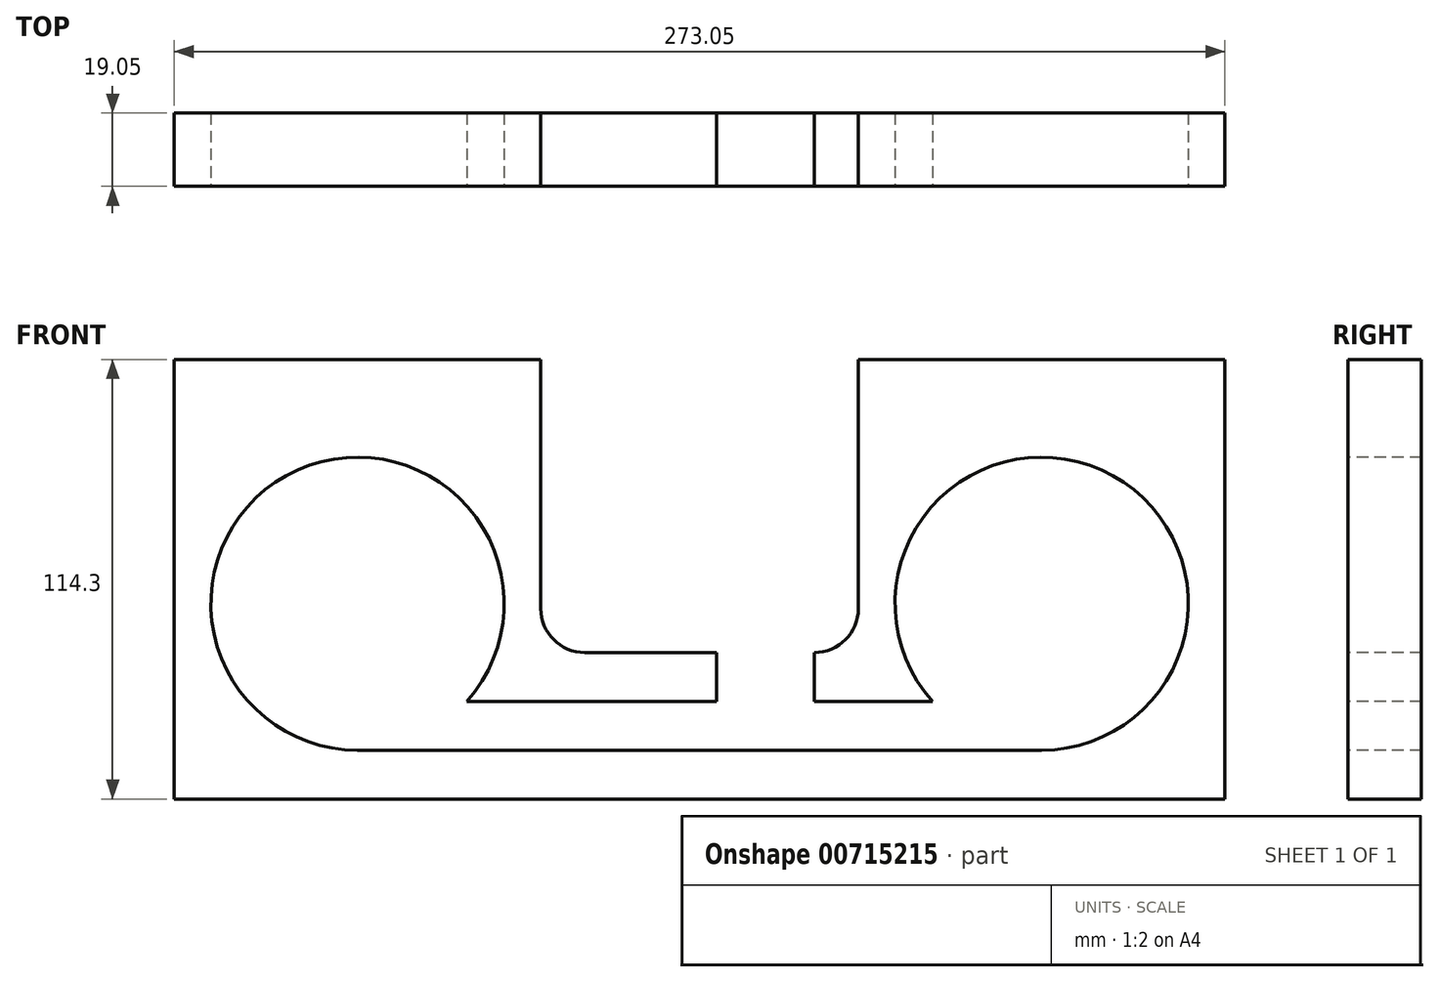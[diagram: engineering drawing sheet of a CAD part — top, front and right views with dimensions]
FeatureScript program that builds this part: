
annotation { "Feature Type Name" : "Feature", "Feature Type Description" : "" }
export const myFeature = defineFeature(function(context is Context, id is Id, definition is map)
    precondition{}
    {
        {
            var Q0;
            Q0=qCreatedBy(makeId("Front.planeOp"),FACE);
            var sketch = newSketch(context, id + "F0", { "sketchPlane" : qUnion([Q0])});
            skLineSegment(sketch, "E0.bottom", {"start": v(0, 0) * mm, "end": v(273.05, 0) * mm});
            skLineSegment(sketch, "E0.top", {"start": v(0, 114.3) * mm, "end": v(273.05, 114.3) * mm});
            skLineSegment(sketch, "E0.left", {"start": v(0, 0) * mm, "end": v(0, 114.3) * mm});
            skLineSegment(sketch, "E0.right", {"start": v(273.05, 0) * mm, "end": v(273.05, 114.3) * mm});
            skSolve(sketch);
        }
        {
            var Q0;
            Q0 = qSketchRegion(id + "F0", true);
            extrude(context, id + "F1", {"entities" : qUnion([Q0]), "depth" : 19.05 * mm, "offsetDistance" : 25.4 * mm});
        }
        {
            var Q0;
            Q0=makeQuery(id+"F1.opExtrude","CAP_FACE",FACE,{"disambiguationData":[OSD([sQuery(id+"F0.wireOp",EDGE,"E0.bottom"),sQuery(id+"F0.wireOp",EDGE,"E0.top"),sQuery(id+"F0.wireOp",EDGE,"E0.left"),sQuery(id+"F0.wireOp",EDGE,"E0.right")])],"isStart":false});
            var sketch = newSketch(context, id + "F2", { "sketchPlane" : qUnion([Q0])});
            skCircle(sketch, "E1", {"center": v(47.63, 50.8) * mm, "radius": 38.1 * mm});
            skCircle(sketch, "E2", {"center": v(225.43, 50.8) * mm, "radius": 38.1 * mm});
            skSolve(sketch);
        }
        {
            var Q0;
            Q0 = qSketchRegion(id + "F2", true);
            extrude(context, id + "F3", {"entities" : qUnion([Q0]), "operationType" : NewBodyOperationType.REMOVE, "oppositeDirection" : true, "depth" : 25.4 * mm, "offsetDistance" : 25.4 * mm});
        }
        {
            var Q0;
            Q0=makeQuery(id+"F1.opExtrude","CAP_FACE",FACE,{"disambiguationData":[OSD([sQuery(id+"F0.wireOp",EDGE,"E0.bottom"),sQuery(id+"F0.wireOp",EDGE,"E0.top"),sQuery(id+"F0.wireOp",EDGE,"E0.left"),sQuery(id+"F0.wireOp",EDGE,"E0.right")])],"isStart":false});
            var sketch = newSketch(context, id + "F4", { "sketchPlane" : qUnion([Q0])});
            skLineSegment(sketch, "E3", {"start": v(95.25, 114.3) * mm, "end": v(95.25, 49.53) * mm});
            skLineSegment(sketch, "E4", {"start": v(106.68, 38.1) * mm, "end": v(166.37, 38.1) * mm});
            skLineSegment(sketch, "E5", {"start": v(177.8, 49.53) * mm, "end": v(177.8, 114.3) * mm});
            skPoint(sketch, "E6.visualSharp", {"position": v(95.25, 38.1) * mm});
            skArc(sketch, "E6.filletArc", {"start": v(95.25, 49.53) * mm, "mid": v(98.6, 41.45) * mm, "end": v(106.68, 38.1) * mm});
            skPoint(sketch, "E7.visualSharp", {"position": v(177.8, 38.1) * mm});
            skArc(sketch, "E7.filletArc", {"start": v(166.37, 38.1) * mm, "mid": v(174.45, 41.45) * mm, "end": v(177.8, 49.53) * mm});
            skSolve(sketch);
        }
        {
            var Q0;
            Q0 = qSketchRegion(id + "F4", true);
            var Q1;
            {var subQ1=sQuery(id+"F4.wireOp",EDGE,"E3");Q1=makeQuery(id+"F4.imprint","IMPRINT",FACE,{"disambiguationData":[TD([[makeQuery(id+"F4.imprint","IMPRINT",EDGE,{"derivedFrom":subQ1}),1.0]])]});}
            extrude(context, id + "F5", {"entities" : qUnion([Q0, Q1]), "operationType" : NewBodyOperationType.REMOVE, "oppositeDirection" : true, "depth" : 25.4 * mm, "offsetDistance" : 25.4 * mm});
        }
        {
            var Q0;
            Q0=makeQuery(id+"F1.opExtrude","CAP_FACE",FACE,{"disambiguationData":[OSD([sQuery(id+"F0.wireOp",EDGE,"E0.bottom"),sQuery(id+"F0.wireOp",EDGE,"E0.top"),sQuery(id+"F0.wireOp",EDGE,"E0.left"),sQuery(id+"F0.wireOp",EDGE,"E0.right")])],"isStart":false});
            var sketch = newSketch(context, id + "F6", { "sketchPlane" : qUnion([Q0])});
            skLineSegment(sketch, "E8", {"start": v(140.97, 38.1) * mm, "end": v(140.97, 25.4) * mm});
            skLineSegment(sketch, "E9", {"start": v(140.97, 25.4) * mm, "end": v(76.02, 25.4) * mm});
            skLineSegment(sketch, "E10", {"start": v(225.43, 12.7) * mm, "end": v(197.03, 25.4) * mm});
            skLineSegment(sketch, "E11", {"start": v(197.03, 25.4) * mm, "end": v(166.37, 25.4) * mm});
            skLineSegment(sketch, "E12", {"start": v(166.37, 25.4) * mm, "end": v(166.37, 38.1) * mm});
            skLineSegment(sketch, "E13", {"start": v(76.02, 25.4) * mm, "end": v(47.63, 12.7) * mm});
            skLineSegment(sketch, "E14", {"start": v(47.63, 12.7) * mm, "end": v(225.43, 12.7) * mm});
            skSolve(sketch);
        }
        {
            var Q0;
            Q0 = qSketchRegion(id + "F6", true);
            var Q1;
            {var subQ3=sQuery(id+"F6.wireOp",EDGE,"E8");Q1=makeQuery(id+"F6.imprint","IMPRINT",FACE,{"disambiguationData":[TD([[makeQuery(id+"F6.imprint","IMPRINT",EDGE,{"derivedFrom":subQ3}),1.0]])]});}
            extrude(context, id + "F7", {"entities" : qUnion([Q0, Q1]), "operationType" : NewBodyOperationType.REMOVE, "oppositeDirection" : true, "depth" : 25.4 * mm, "offsetDistance" : 25.4 * mm});
        }
    });
